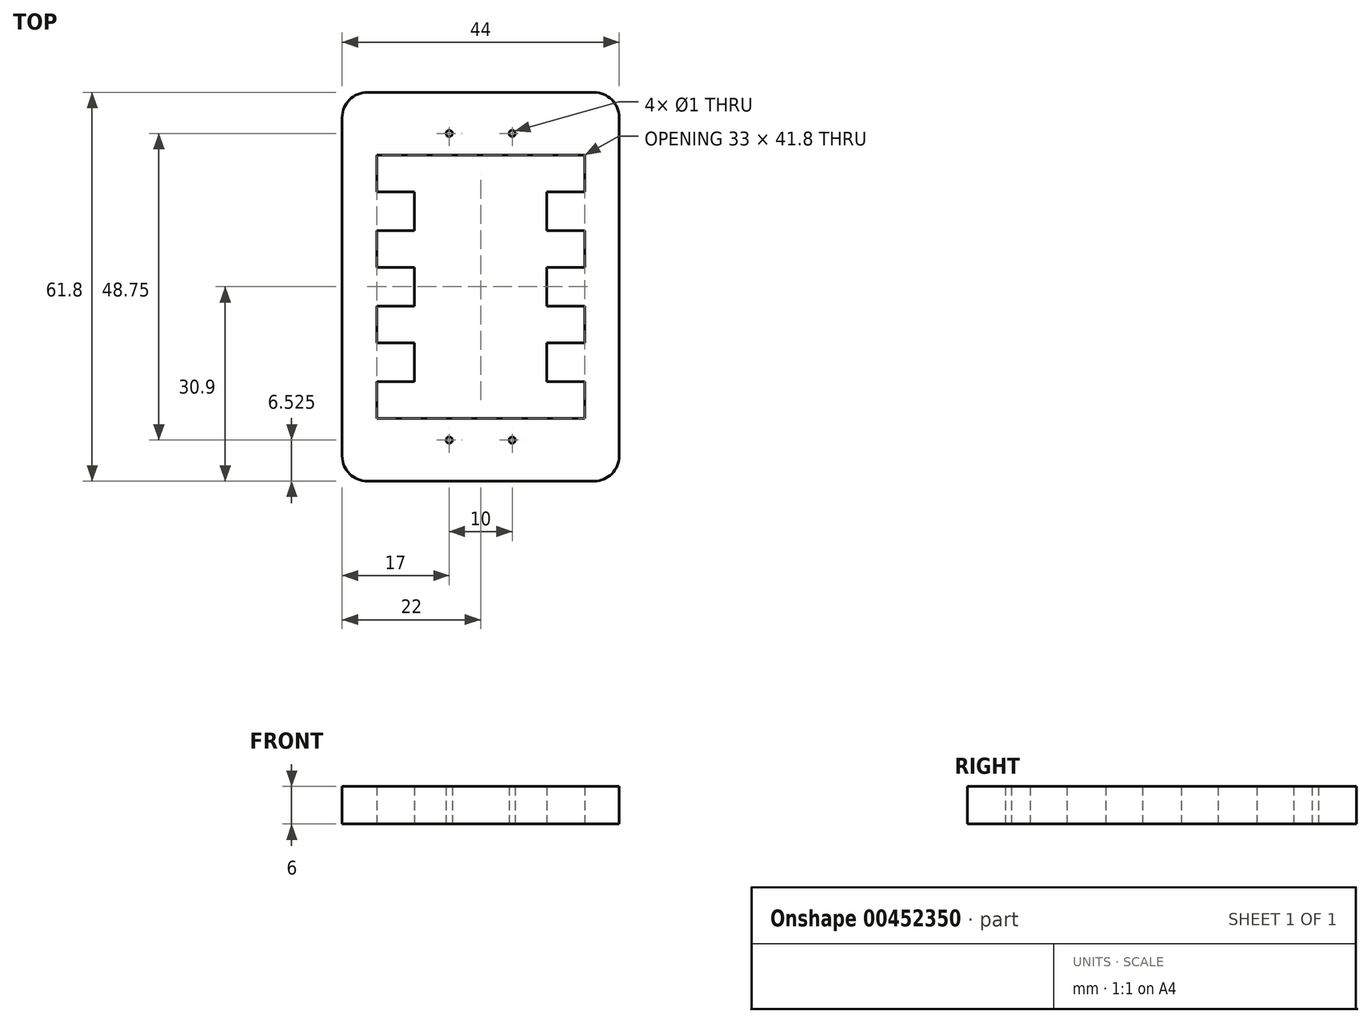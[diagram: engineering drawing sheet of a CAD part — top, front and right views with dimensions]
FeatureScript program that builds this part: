
annotation { "Feature Type Name" : "Feature", "Feature Type Description" : "" }
export const myFeature = defineFeature(function(context is Context, id is Id, definition is map)
    precondition{}
    {
        {
            var Q0;
            Q0=qCreatedBy(makeId("Top.planeOp"),FACE);
            var sketch = newSketch(context, id + "F0", { "sketchPlane" : qUnion([Q0])});
            skLineSegment(sketch, "E0.bottom", {"start": v(-18, 30.9) * mm, "end": v(18, 30.9) * mm});
            skLineSegment(sketch, "E0.top", {"start": v(-18, -30.9) * mm, "end": v(18, -30.9) * mm});
            skLineSegment(sketch, "E0.left", {"start": v(-22, 26.9) * mm, "end": v(-22, -26.9) * mm});
            skLineSegment(sketch, "E0.right", {"start": v(22, 26.9) * mm, "end": v(22, -26.9) * mm});
            skLineSegment(sketch, "E1.bottom", {"start": v(-10.5, 20.9) * mm, "end": v(10.5, 20.9) * mm});
            skLineSegment(sketch, "E1.top", {"start": v(-10.5, -20.9) * mm, "end": v(10.5, -20.9) * mm});
            skCircle(sketch, "E2", {"center": v(-5, -24.38) * mm, "radius": 0.5 * mm});
            skCircle(sketch, "E3", {"center": v(5, -24.38) * mm, "radius": 0.5 * mm});
            skCircle(sketch, "E4", {"center": v(-5, 24.38) * mm, "radius": 0.5 * mm});
            skCircle(sketch, "E5", {"center": v(5, 24.38) * mm, "radius": 0.5 * mm});
            skPoint(sketch, "E6.visualSharp", {"position": v(-22, 30.9) * mm});
            skArc(sketch, "E6.filletArc", {"start": v(-18, 30.9) * mm, "mid": v(-20.83, 29.73) * mm, "end": v(-22, 26.9) * mm});
            skPoint(sketch, "E7.visualSharp", {"position": v(22, 30.9) * mm});
            skArc(sketch, "E7.filletArc", {"start": v(22, 26.9) * mm, "mid": v(20.83, 29.73) * mm, "end": v(18, 30.9) * mm});
            skPoint(sketch, "E8.visualSharp", {"position": v(22, -30.9) * mm});
            skArc(sketch, "E8.filletArc", {"start": v(18, -30.9) * mm, "mid": v(20.83, -29.73) * mm, "end": v(22, -26.9) * mm});
            skPoint(sketch, "E9.visualSharp", {"position": v(-22, -30.9) * mm});
            skArc(sketch, "E9.filletArc", {"start": v(-22, -26.9) * mm, "mid": v(-20.83, -29.73) * mm, "end": v(-18, -30.9) * mm});
            skLineSegment(sketch, "E10", {"start": v(-10.5, 20.9) * mm, "end": v(-16.5, 20.9) * mm});
            skLineSegment(sketch, "E11", {"start": v(-16.5, 20.9) * mm, "end": v(-16.5, 15.1) * mm});
            skLineSegment(sketch, "E12", {"start": v(-16.5, 15.1) * mm, "end": v(-10.5, 15.1) * mm});
            skLineSegment(sketch, "E13", {"start": v(-10.5, 15.1) * mm, "end": v(-10.5, 8.9) * mm});
            skLineSegment(sketch, "E14", {"start": v(-10.5, 8.9) * mm, "end": v(-16.5, 8.9) * mm});
            skLineSegment(sketch, "E15", {"start": v(-16.5, 8.9) * mm, "end": v(-16.5, 3.1) * mm});
            skLineSegment(sketch, "E16", {"start": v(-16.5, 3.1) * mm, "end": v(-10.5, 3.1) * mm});
            skLineSegment(sketch, "E17", {"start": v(-10.5, 3.1) * mm, "end": v(-10.5, -3.1) * mm});
            skLineSegment(sketch, "E18", {"start": v(-10.5, -3.1) * mm, "end": v(-16.5, -3.1) * mm});
            skLineSegment(sketch, "E19", {"start": v(-16.5, -3.1) * mm, "end": v(-16.5, -8.9) * mm});
            skLineSegment(sketch, "E20", {"start": v(-16.5, -8.9) * mm, "end": v(-10.5, -8.9) * mm});
            skLineSegment(sketch, "E21", {"start": v(-10.5, -8.9) * mm, "end": v(-10.5, -15.1) * mm});
            skLineSegment(sketch, "E22", {"start": v(-10.5, -15.1) * mm, "end": v(-16.5, -15.1) * mm});
            skLineSegment(sketch, "E23", {"start": v(-16.5, -15.1) * mm, "end": v(-16.5, -20.9) * mm});
            skLineSegment(sketch, "E24", {"start": v(-16.5, -20.9) * mm, "end": v(-10.5, -20.9) * mm});
            skLineSegment(sketch, "E25.MirrorCS", {"start": v(10.5, -3.1) * mm, "end": v(16.5, -3.1) * mm});
            skLineSegment(sketch, "E26.MirrorCS", {"start": v(10.5, 8.9) * mm, "end": v(16.5, 8.9) * mm});
            skLineSegment(sketch, "E27.MirrorCS", {"start": v(10.5, 3.1) * mm, "end": v(10.5, -3.1) * mm});
            skLineSegment(sketch, "E28.MirrorCS", {"start": v(16.5, 20.9) * mm, "end": v(16.5, 15.1) * mm});
            skLineSegment(sketch, "E29.MirrorCS", {"start": v(10.5, -15.1) * mm, "end": v(16.5, -15.1) * mm});
            skLineSegment(sketch, "E30.MirrorCS", {"start": v(16.5, -20.9) * mm, "end": v(10.5, -20.9) * mm});
            skLineSegment(sketch, "E31.MirrorCS", {"start": v(16.5, -8.9) * mm, "end": v(10.5, -8.9) * mm});
            skLineSegment(sketch, "E32.MirrorCS", {"start": v(16.5, -15.1) * mm, "end": v(16.5, -20.9) * mm});
            skLineSegment(sketch, "E33.MirrorCS", {"start": v(10.5, -8.9) * mm, "end": v(10.5, -15.1) * mm});
            skLineSegment(sketch, "E34.MirrorCS", {"start": v(16.5, 3.1) * mm, "end": v(10.5, 3.1) * mm});
            skLineSegment(sketch, "E35.MirrorCS", {"start": v(16.5, 15.1) * mm, "end": v(10.5, 15.1) * mm});
            skLineSegment(sketch, "E36.MirrorCS", {"start": v(10.5, 15.1) * mm, "end": v(10.5, 8.9) * mm});
            skLineSegment(sketch, "E37.MirrorCS", {"start": v(10.5, 20.9) * mm, "end": v(16.5, 20.9) * mm});
            skLineSegment(sketch, "E38.MirrorCS", {"start": v(16.5, -3.1) * mm, "end": v(16.5, -8.9) * mm});
            skLineSegment(sketch, "E39.MirrorCS", {"start": v(16.5, 8.9) * mm, "end": v(16.5, 3.1) * mm});
            skSolve(sketch);
        }
        {
            var Q0;
            Q0 = qSketchRegion(id + "F0", true);
            extrude(context, id + "F1", {"entities" : qUnion([Q0]), "depth" : 6 * mm});
        }
    });
